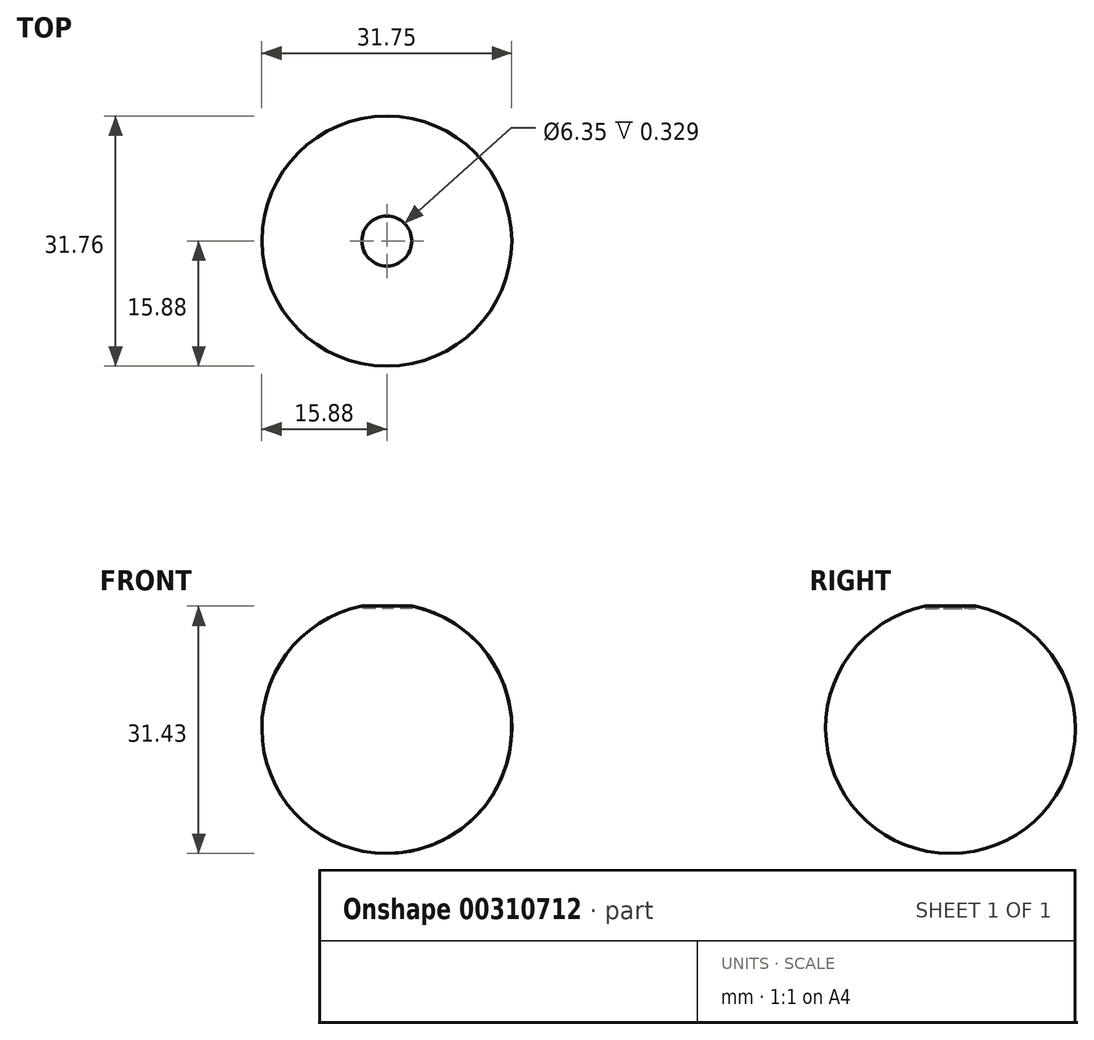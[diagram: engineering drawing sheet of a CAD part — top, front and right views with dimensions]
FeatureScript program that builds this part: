
annotation { "Feature Type Name" : "Feature", "Feature Type Description" : "" }
export const myFeature = defineFeature(function(context is Context, id is Id, definition is map)
    precondition{}
    {
        {
            var Q0;
            Q0=qCreatedBy(makeId("Front.planeOp"),FACE);
            var sketch = newSketch(context, id + "F0", { "sketchPlane" : qUnion([Q0])});
            skArc(sketch, "E0", {"start": v(0, 15.88) * mm, "mid": v(-15.88, 0) * mm, "end": v(0, -15.88) * mm});
            skLineSegment(sketch, "E1", {"start": v(0, 15.88) * mm, "end": v(0, -15.88) * mm});
            skSolve(sketch);
        }
        {
            var Q0;
            Q0=qCreatedBy(makeId("Top.planeOp"),FACE);
            var sketch = newSketch(context, id + "F1", { "sketchPlane" : qUnion([Q0])});
            skCircle(sketch, "E2", {"center": v(0, 0) * mm, "radius": 15.88 * mm});
            skSolve(sketch);
        }
        {
            var Q0;
            Q0=makeQuery(id+"F0.imprint","IMPRINT",FACE,{"disambiguationData":[TD([[makeQuery(id+"F0.imprint","IMPRINT",EDGE,{"derivedFrom":sQuery(id+"F0.wireOp",EDGE,"E0")}),1.0]])]});
            var Q1;
            Q1=sQuery(id+"F1.wireOp",EDGE,"E2");
            revolve(context, id + "F2", {"entities" : qUnion([Q0]), "axis" : qUnion([Q1]), "revolveType" : RevolveType.FULL});
        }
        {
            var Q0;
            Q0=qCreatedBy(makeId("Top.planeOp"),FACE);
            cPlane(context, id + "F3", {"entities" : qUnion([Q0]), "cplaneType" : CPlaneType.OFFSET, "offset" : 15.24 * mm, "width" : 152.4 * mm, "height" : 152.4 * mm});
        }
        {
            var Q0;
            Q0=qCreatedBy(id+"F3.planeOp",FACE);
            cPlane(context, id + "F4", {"entities" : qUnion([Q0]), "cplaneType" : CPlaneType.OFFSET, "offset" : 3 / 203.2 * mm, "oppositeDirection" : true, "width" : 152.4 * mm, "height" : 152.4 * mm});
        }
        {
            var Q0;
            Q0=qCreatedBy(id+"F4.planeOp",FACE);
            var sketch = newSketch(context, id + "F5", { "sketchPlane" : qUnion([Q0])});
            skCircle(sketch, "E3", {"center": v(0, 0) * mm, "radius": 3.18 * mm});
            skSolve(sketch);
        }
        {
            var Q0;
            Q0 = qSketchRegion(id + "F5", true);
            extrude(context, id + "F6", {"entities" : qUnion([Q0]), "depth" : 50.8 * mm});
        }
        {
            var Q0;
            Q0=makeQuery(id+"F6.opExtrude","SWEPT_BODY",BODY,{"disambiguationData":[OSD([sQuery(id+"F5.wireOp",EDGE,"E3")])]});
            var Q1;
            Q1=makeQuery(id+"F2.opRevolve","SWEPT_BODY",BODY,{"disambiguationData":[OSD([sQuery(id+"F0.wireOp",EDGE,"E0"),sQuery(id+"F0.wireOp",EDGE,"E1")])]});
            booleanBodies(context, id + "F7", {"operationType" : BooleanOperationType.SUBTRACTION, "tools" : qUnion([Q0]), "targets" : qUnion([Q1])});
        }
    });
